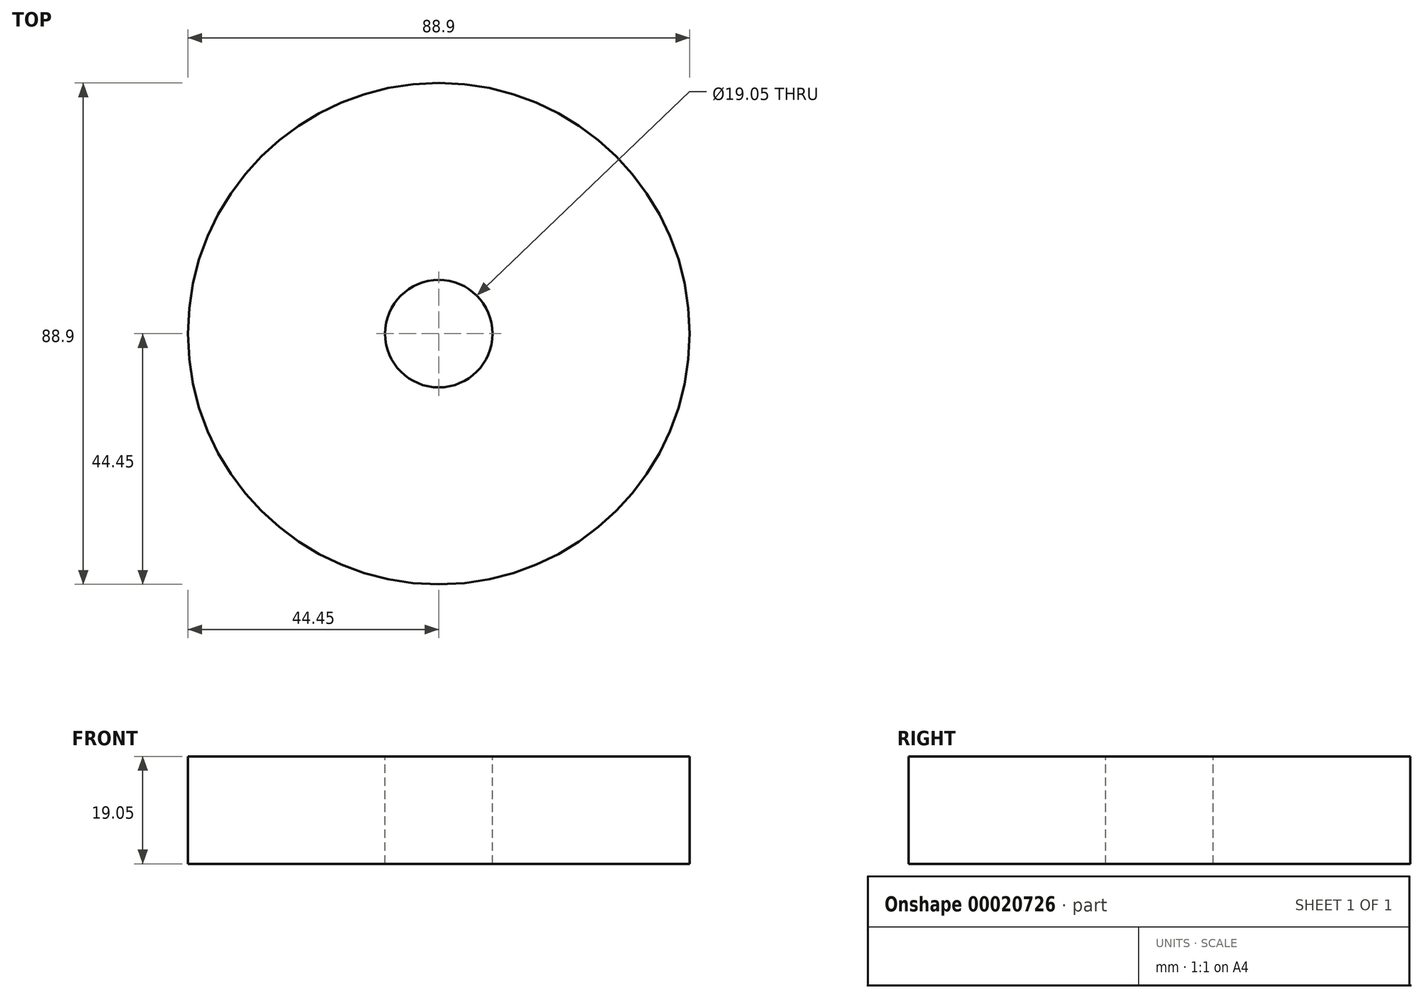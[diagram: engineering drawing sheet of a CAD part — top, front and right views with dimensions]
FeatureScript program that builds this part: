
annotation { "Feature Type Name" : "Feature", "Feature Type Description" : "" }
export const myFeature = defineFeature(function(context is Context, id is Id, definition is map)
    precondition{}
    {
        {
            var Q0;
            Q0=qCreatedBy(makeId("Front.planeOp"),FACE);
            var sketch = newSketch(context, id + "F0", { "sketchPlane" : qUnion([Q0])});
            skLineSegment(sketch, "E0.bottom", {"start": v(-44.45, -41.7) * mm, "end": v(-9.52, -41.7) * mm});
            skLineSegment(sketch, "E0.top", {"start": v(-44.45, -60.75) * mm, "end": v(-9.52, -60.75) * mm});
            skLineSegment(sketch, "E0.left", {"start": v(-44.45, -41.7) * mm, "end": v(-44.45, -60.75) * mm});
            skLineSegment(sketch, "E0.right", {"start": v(-9.52, -41.7) * mm, "end": v(-9.52, -60.75) * mm});
            skLineSegment(sketch, "E1", {"start": v(0, 77.04) * mm, "end": v(0, -80.59) * mm});
            skLineSegment(sketch, "E2.bottom", {"start": v(-9.52, -41.7) * mm, "end": v(-25.4, -41.7) * mm});
            skLineSegment(sketch, "E2.top", {"start": v(-9.52, 15.45) * mm, "end": v(-25.4, 15.45) * mm});
            skLineSegment(sketch, "E2.left", {"start": v(-9.52, -41.7) * mm, "end": v(-9.52, 15.45) * mm});
            skLineSegment(sketch, "E2.right", {"start": v(-25.4, -41.7) * mm, "end": v(-25.4, 15.45) * mm});
            skLineSegment(sketch, "E3.bottom", {"start": v(-9.52, 15.45) * mm, "end": v(-19.05, 15.45) * mm});
            skLineSegment(sketch, "E3.top", {"start": v(-9.52, 28.15) * mm, "end": v(-19.05, 28.15) * mm});
            skLineSegment(sketch, "E3.left", {"start": v(-9.52, 15.45) * mm, "end": v(-9.52, 28.15) * mm});
            skLineSegment(sketch, "E3.right", {"start": v(-19.05, 15.45) * mm, "end": v(-19.05, 28.15) * mm});
            skSolve(sketch);
        }
        {
            var Q0;
            Q0=makeQuery(id+"F0.imprint","IMPRINT",FACE,{"disambiguationData":[TD([[makeQuery(id+"F0.imprint","IMPRINT",EDGE,{"derivedFrom":sQuery(id+"F0.wireOp",EDGE,"E0.bottom")}),-1.0]])]});
            var Q1;
            Q1=makeQuery(id+"F0.imprint","IMPRINT",FACE,{"disambiguationData":[TD([[makeQuery(id+"F0.imprint","IMPRINT",EDGE,{"derivedFrom":sQuery(id+"F0.wireOp",EDGE,"E2.bottom")}),-1.0]])]});
            var Q2;
            Q2=makeQuery(id+"F0.imprint","IMPRINT",FACE,{"disambiguationData":[TD([[makeQuery(id+"F0.imprint","IMPRINT",EDGE,{"derivedFrom":sQuery(id+"F0.wireOp",EDGE,"E3.bottom")}),-1.0]])]});
            var Q3;
            Q3=sQuery(id+"F0.wireOp",EDGE,"E1");
            revolve(context, id + "F1", {"entities" : qUnion([Q0, Q1, Q2]), "axis" : qUnion([Q3]), "revolveType" : RevolveType.FULL});
        }
    });
